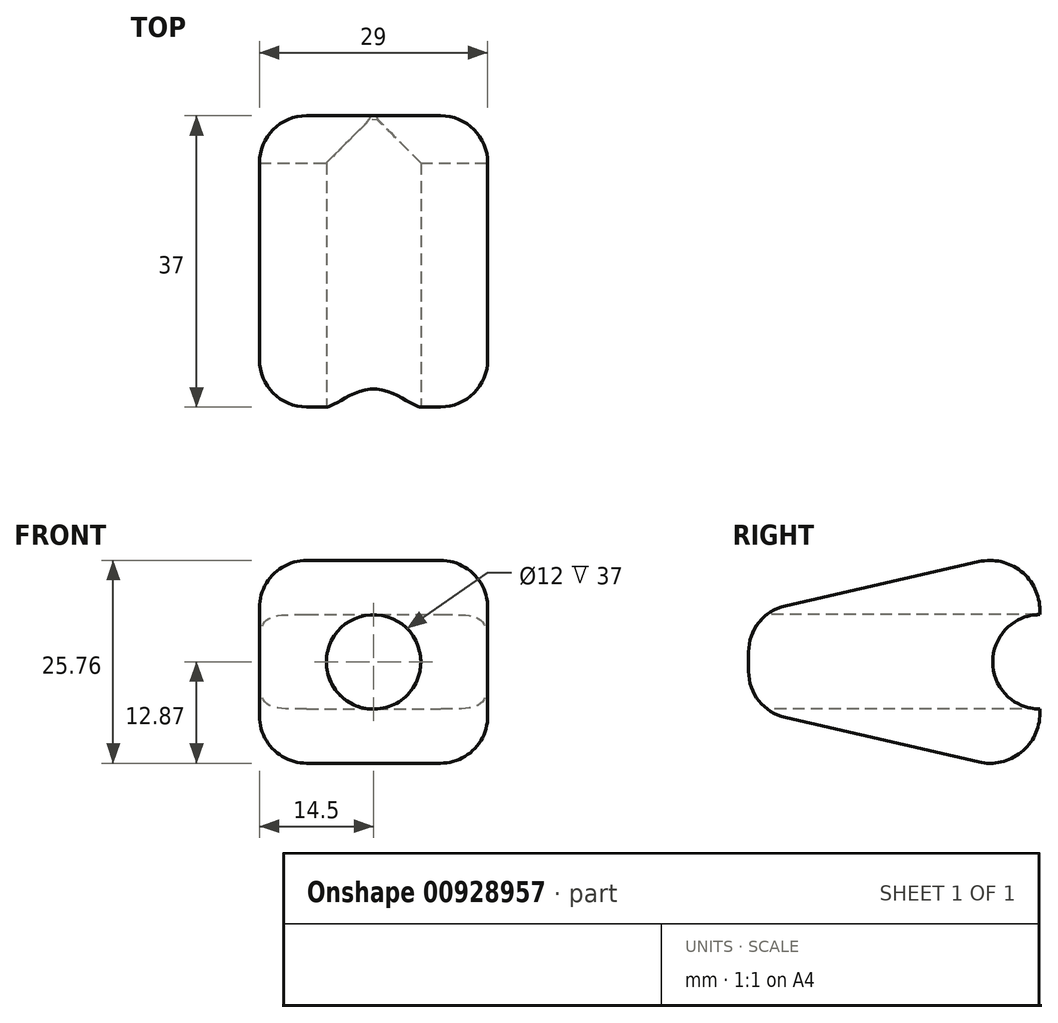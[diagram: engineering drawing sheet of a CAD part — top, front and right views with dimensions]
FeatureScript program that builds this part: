
annotation { "Feature Type Name" : "Feature", "Feature Type Description" : "" }
export const myFeature = defineFeature(function(context is Context, id is Id, definition is map)
    precondition{}
    {
        {
            var Q0;
            Q0=qCreatedBy(makeId("Front.planeOp"),FACE);
            var sketch = newSketch(context, id + "F0", { "sketchPlane" : qUnion([Q0])});
            skCircle(sketch, "E0", {"center": v(0, 0) * mm, "radius": 6 * mm});
            skSolve(sketch);
        }
        {
            var Q0;
            Q0=qCreatedBy(makeId("Right.planeOp"),FACE);
            var sketch = newSketch(context, id + "F1", { "sketchPlane" : qUnion([Q0])});
            skLineSegment(sketch, "E1", {"start": v(0, 6.07) * mm, "end": v(29.24, 12.73) * mm});
            skLineSegment(sketch, "E2", {"start": v(37, 6.54) * mm, "end": v(37, -6.52) * mm});
            skLineSegment(sketch, "E3", {"start": v(29.23, -12.71) * mm, "end": v(0, -6) * mm});
            skLineSegment(sketch, "E4", {"start": v(-19.43, 0) * mm, "end": v(101.93, 0) * mm, "construction": true});
            skPoint(sketch, "E5.visualSharp", {"position": v(37, 14.5) * mm});
            skArc(sketch, "E5.filletArc", {"start": v(37, 6.54) * mm, "mid": v(34.61, 11.5) * mm, "end": v(29.24, 12.73) * mm});
            skPoint(sketch, "E6.visualSharp", {"position": v(37, -14.5) * mm});
            skArc(sketch, "E6.filletArc", {"start": v(29.23, -12.71) * mm, "mid": v(34.6, -11.5) * mm, "end": v(37, -6.52) * mm});
            skLineSegment(sketch, "E7", {"start": v(0, 6.07) * mm, "end": v(0, -6) * mm});
            skSolve(sketch);
        }
        {
            var Q0;
            Q0 = qSketchRegion(id + "F1", true);
            extrude(context, id + "F2", {"entities" : qUnion([Q0]), "endBound" : BoundingType.SYMMETRIC, "depth" : 29 * mm, "offsetDistance" : 25.4 * mm});
        }
        {
            var Q0;
            Q0=makeQuery(id+"F2.opExtrude","CAP_FACE",FACE,{"disambiguationData":[OSD([sQuery(id+"F1.wireOp",EDGE,"E1"),sQuery(id+"F1.wireOp",EDGE,"E2"),sQuery(id+"F1.wireOp",EDGE,"E3"),sQuery(id+"F1.wireOp",EDGE,"E5.filletArc"),sQuery(id+"F1.wireOp",EDGE,"E6.filletArc"),sQuery(id+"F1.wireOp",EDGE,"E7")])],"isStart":false});
            var sketch = newSketch(context, id + "F3", { "sketchPlane" : qUnion([Q0])});
            skArc(sketch, "E8", {"start": v(37, 6) * mm, "mid": v(31, 0) * mm, "end": v(37, -6) * mm});
            skLineSegment(sketch, "E9", {"start": v(37, 6) * mm, "end": v(37, -6) * mm});
            skSolve(sketch);
        }
        {
            var Q0;
            Q0 = qSketchRegion(id + "F3", true);
            extrude(context, id + "F4", {"entities" : qUnion([Q0]), "operationType" : NewBodyOperationType.REMOVE, "endBound" : BoundingType.THROUGH_ALL, "oppositeDirection" : true, "depth" : 25.4 * mm, "offsetDistance" : 25.4 * mm});
        }
        {
            var Q0;
            Q0=makeQuery(id+"F2.opExtrude","CAP_EDGE",EDGE,{"disambiguationData":[OSD([sQuery(id+"F1.wireOp",EDGE,"E1")])],"isStart":false});
            var Q1;
            Q1=makeQuery(id+"F2.opExtrude","CAP_EDGE",EDGE,{"disambiguationData":[OSD([sQuery(id+"F1.wireOp",EDGE,"E3")])],"isStart":false});
            var Q2;
            Q2=makeQuery(id+"F2.opExtrude","SWEPT_EDGE",EDGE,{"disambiguationData":[OSD([sQuery(id+"F1.wireOp",EDGE,"E2"),sQuery(id+"F1.wireOp",EDGE,"E5.filletArc")])]});
            var Q3;
            Q3=makeQuery(id+"F2.opExtrude","CAP_EDGE",EDGE,{"disambiguationData":[OSD([sQuery(id+"F1.wireOp",EDGE,"E1")])],"isStart":true});
            var Q4;
            Q4=makeQuery(id+"F2.opExtrude","CAP_EDGE",EDGE,{"disambiguationData":[OSD([sQuery(id+"F1.wireOp",EDGE,"E3")])],"isStart":true});
            var Q5;
            Q5=makeQuery(id+"F2.opExtrude","SWEPT_EDGE",EDGE,{"disambiguationData":[OSD([sQuery(id+"F1.wireOp",EDGE,"E3"),sQuery(id+"F1.wireOp",EDGE,"E7")])]});
            var Q6;
            Q6=makeQuery(id+"F2.opExtrude","SWEPT_EDGE",EDGE,{"disambiguationData":[OSD([sQuery(id+"F1.wireOp",EDGE,"E1"),sQuery(id+"F1.wireOp",EDGE,"E7")])]});
            var Q7;
            Q7=makeQuery(id+"F2.opExtrude","CAP_EDGE",EDGE,{"disambiguationData":[OSD([sQuery(id+"F1.wireOp",EDGE,"E7")])],"isStart":false});
            var Q8;
            Q8=makeQuery(id+"F2.opExtrude","CAP_EDGE",EDGE,{"disambiguationData":[OSD([sQuery(id+"F1.wireOp",EDGE,"E7")])],"isStart":true});
            fillet(context, id + "F5", {"entities" : qUnion([Q0, Q1, Q2, Q3, Q4, Q5, Q6, Q7, Q8]), "radius" : 6 * mm, "tangentPropagation" : true, "allowEdgeOverflow" : false});
        }
        {
            var Q0;
            Q0 = qSketchRegion(id + "F0", true);
            extrude(context, id + "F6", {"entities" : qUnion([Q0]), "operationType" : NewBodyOperationType.REMOVE, "oppositeDirection" : true, "depth" : 87.12 * mm, "offsetDistance" : 25.4 * mm});
        }
    });
